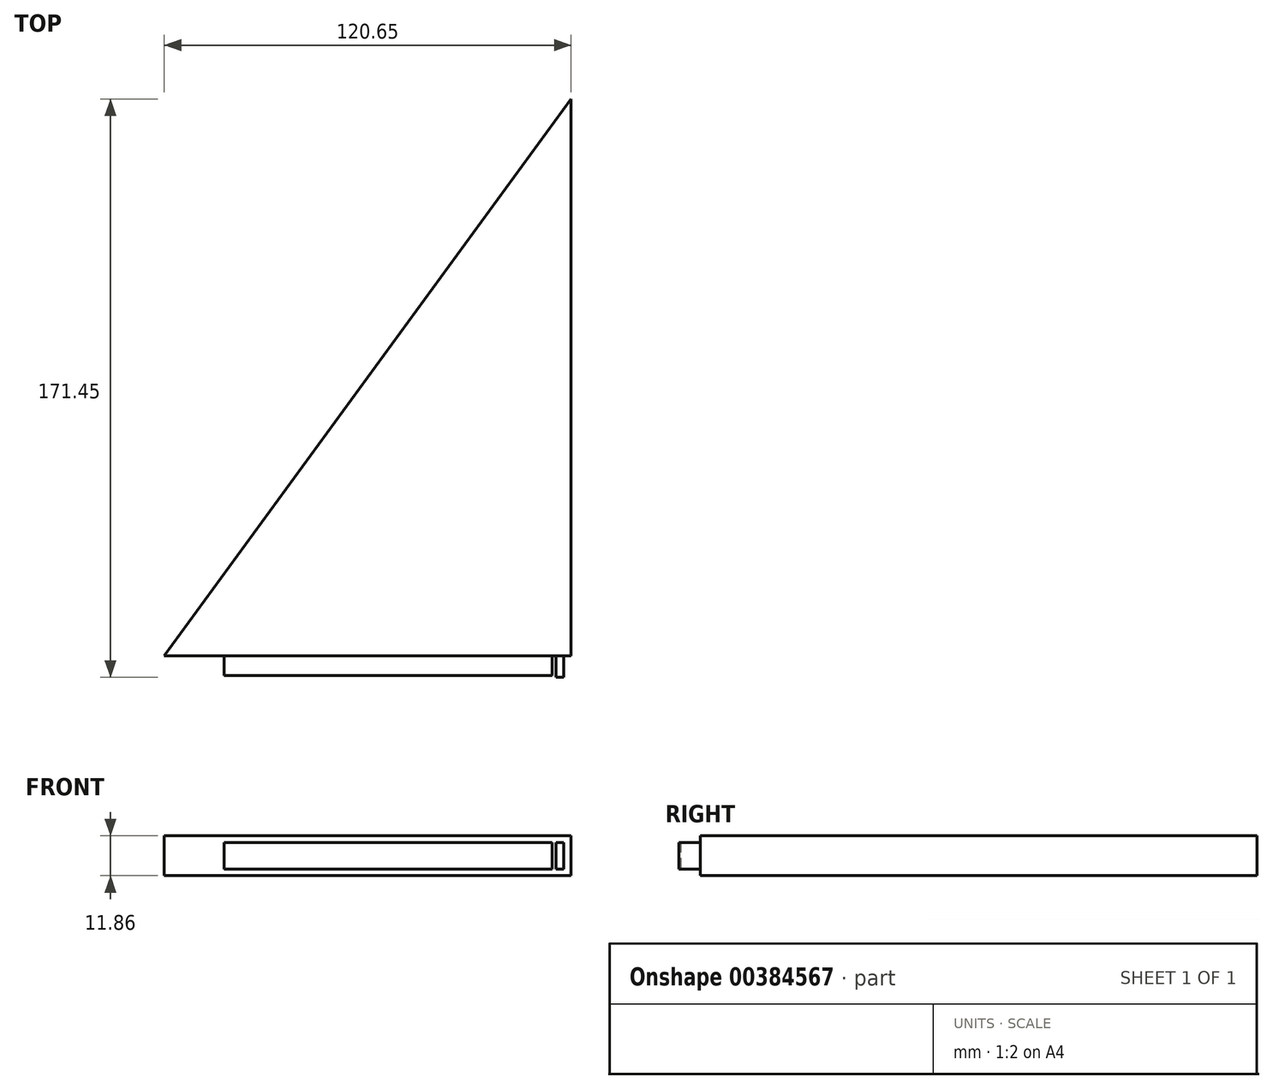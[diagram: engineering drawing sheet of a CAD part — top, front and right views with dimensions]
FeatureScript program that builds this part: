
annotation { "Feature Type Name" : "Feature", "Feature Type Description" : "" }
export const myFeature = defineFeature(function(context is Context, id is Id, definition is map)
    precondition{}
    {
        {
            var Q0;
            Q0=qCreatedBy(makeId("Top.planeOp"),FACE);
            var sketch = newSketch(context, id + "F0", { "sketchPlane" : qUnion([Q0])});
            skLineSegment(sketch, "E0", {"start": v(0, 0) * mm, "end": v(0, 165.1) * mm});
            skLineSegment(sketch, "E1", {"start": v(0, 165.1) * mm, "end": v(-120.65, 0) * mm});
            skLineSegment(sketch, "E2", {"start": v(-120.65, 0) * mm, "end": v(0, 0) * mm});
            skSolve(sketch);
        }
        {
            var Q0;
            Q0=makeQuery(id+"F0.imprint","IMPRINT",FACE,{"disambiguationData":[TD([[makeQuery(id+"F0.imprint","IMPRINT",EDGE,{"derivedFrom":sQuery(id+"F0.wireOp",EDGE,"E0")}),1.0]])]});
            extrude(context, id + "F1", {"entities" : qUnion([Q0]), "depth" : 11.86 * mm});
        }
        {
            var Q0;
            Q0=makeQuery(id+"F1.opExtrude","SWEPT_FACE",FACE,{"disambiguationData":[OSD([sQuery(id+"F0.wireOp",EDGE,"E2")])]});
            var sketch = newSketch(context, id + "F2", { "sketchPlane" : qUnion([Q0])});
            skLineSegment(sketch, "E3.bottom", {"start": v(-102.87, 9.87) * mm, "end": v(-5.59, 9.87) * mm});
            skLineSegment(sketch, "E3.top", {"start": v(-102.87, 2) * mm, "end": v(-5.59, 2) * mm});
            skLineSegment(sketch, "E3.left", {"start": v(-102.87, 9.87) * mm, "end": v(-102.87, 2) * mm});
            skLineSegment(sketch, "E3.right", {"start": v(-5.59, 9.87) * mm, "end": v(-5.59, 2) * mm});
            skSolve(sketch);
        }
        {
            var Q0;
            Q0=makeQuery(id+"F2.imprint","IMPRINT",FACE,{"disambiguationData":[TD([[makeQuery(id+"F2.imprint","IMPRINT",EDGE,{"derivedFrom":sQuery(id+"F2.wireOp",EDGE,"E3.bottom")}),-1.0]])]});
            extrude(context, id + "F3", {"entities" : qUnion([Q0]), "operationType" : NewBodyOperationType.ADD, "depth" : 5.84 * mm});
        }
        {
            var Q0;
            Q0=makeQuery(id+"F1.opExtrude","SWEPT_FACE",FACE,{"disambiguationData":[OSD([sQuery(id+"F0.wireOp",EDGE,"E2")])]});
            var sketch = newSketch(context, id + "F4", { "sketchPlane" : qUnion([Q0])});
            skLineSegment(sketch, "E4.bottom", {"start": v(-4.55, 9.87) * mm, "end": v(-2.27, 9.87) * mm});
            skLineSegment(sketch, "E4.top", {"start": v(-4.55, 2) * mm, "end": v(-2.27, 2) * mm});
            skLineSegment(sketch, "E4.left", {"start": v(-4.55, 9.87) * mm, "end": v(-4.55, 2) * mm});
            skLineSegment(sketch, "E4.right", {"start": v(-2.27, 9.87) * mm, "end": v(-2.27, 2) * mm});
            skSolve(sketch);
        }
        {
            var Q0;
            Q0=makeQuery(id+"F4.imprint","IMPRINT",FACE,{"disambiguationData":[TD([[makeQuery(id+"F4.imprint","IMPRINT",EDGE,{"derivedFrom":sQuery(id+"F4.wireOp",EDGE,"E4.bottom")}),-1.0]])]});
            extrude(context, id + "F5", {"entities" : qUnion([Q0]), "operationType" : NewBodyOperationType.ADD, "depth" : 6.35 * mm});
        }
    });
